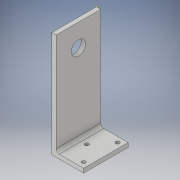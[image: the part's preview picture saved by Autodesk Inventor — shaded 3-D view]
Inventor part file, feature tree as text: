
AUTODESK INVENTOR PART (.ipt)
format: ipt  version: 2017 (Build 210142000, 142)  size: 129,536 bytes
history: native  units: in
note: dims shown in document units (in); Inventor stores cm internally (conversion verified against a paired STEP export)
features: sketch x4, extrude x3, fillet x1
ambient origin geometry x8: Origin, YZ Plane, XZ Plane, XY Plane, X Axis, Y Axis, Z Axis, Center Point
bodies: Solid1 (feature_tree)
feature tree (8):
  sketch  "Sketch1"  dims[d0=3.937in d1=1.1811in]
  extrude  "Extrusion1"  Depth=1.1811in
  extrude  "Extrusion3"  Depth=1.0236in
  fillet  "Fillet1"  Radius=1.6535in
  extrude  "Extrusion4"  Depth=0.1378in
  sketch  "Sketch2"  dims[d2=0.1575in d3=1.0236in d4=1.6535in d5=0.0in]
  sketch  "Sketch4"  dims[d11=0.1378in d12=0.1378in]
  sketch  "Sketch5"  dims[d13=0.1378in d14=0.1969in d15=0.1969in d16=0.1969in d17=0.1969in d18=0.4724in d19=0.8268in d20=0.1575in d21=0.0in d22=0.1181in d23=0.5236in d24=0.8268in d25=0.8268in d26=0.1575in d27=0.0in]
